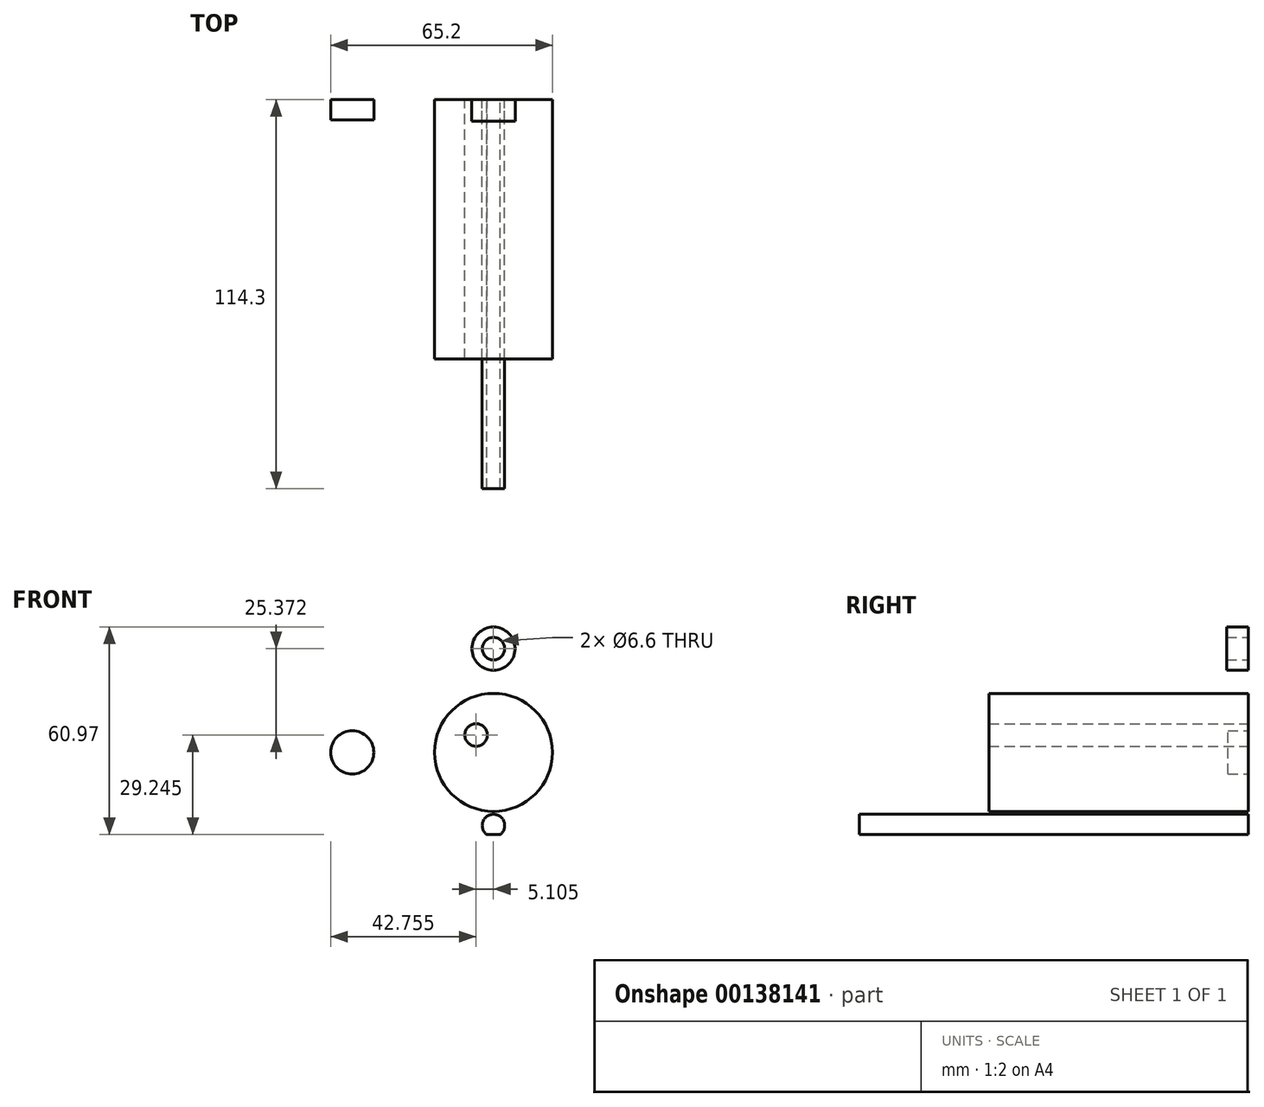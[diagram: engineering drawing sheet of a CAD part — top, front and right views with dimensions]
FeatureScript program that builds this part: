
annotation { "Feature Type Name" : "Feature", "Feature Type Description" : "" }
export const myFeature = defineFeature(function(context is Context, id is Id, definition is map)
    precondition{}
    {
        {
            var Q0;
            Q0=qCreatedBy(makeId("Front.planeOp"),FACE);
            var sketch = newSketch(context, id + "F0", { "sketchPlane" : qUnion([Q0])});
            skCircle(sketch, "E0", {"center": v(0, 0) * mm, "radius": 17.34 * mm});
            skLineSegment(sketch, "E1", {"start": v(0, 0) * mm, "end": v(0, 17.34) * mm, "construction": true});
            skLineSegment(sketch, "E2", {"start": v(0, 0) * mm, "end": v(0, -17.34) * mm, "construction": true});
            skLineSegment(sketch, "E3", {"start": v(-17.34, 0) * mm, "end": v(17.34, 0) * mm, "construction": true});
            skLineSegment(sketch, "E4", {"start": v(-5.1, 0) * mm, "end": v(-5.1, 5.1) * mm});
            skLineSegment(sketch, "E5", {"start": v(-5.1, 5.1) * mm, "end": v(0, 5.1) * mm, "construction": true});
            skCircle(sketch, "E6", {"center": v(-5.1, 5.1) * mm, "radius": 3.3 * mm});
            skSolve(sketch);
        }
        {
            var Q0;
            Q0=qCreatedBy(makeId("Front.planeOp"),FACE);
            var sketch = newSketch(context, id + "F1", { "sketchPlane" : qUnion([Q0])});
            skArc(sketch, "E7", {"start": v(1.98, -24.14) * mm, "mid": v(0, -18.2) * mm, "end": v(-1.98, -24.14) * mm});
            skLineSegment(sketch, "E8", {"start": v(-1.98, -24.14) * mm, "end": v(1.98, -24.14) * mm});
            skSolve(sketch);
        }
        {
            var Q0;
            Q0=makeQuery(id+"F0.imprint","IMPRINT",FACE,{"disambiguationData":[TD([[makeQuery(id+"F0.imprint","IMPRINT",EDGE,{"derivedFrom":sQuery(id+"F0.wireOp",EDGE,"E0")}),1.0]])]});
            extrude(context, id + "F2", {"entities" : qUnion([Q0]), "depth" : 76.2 * mm});
        }
        {
            var Q0;
            Q0=makeQuery(id+"F1.imprint","IMPRINT",FACE,{"disambiguationData":[TD([[makeQuery(id+"F1.imprint","IMPRINT",EDGE,{"derivedFrom":sQuery(id+"F1.wireOp",EDGE,"E7")}),1.0]])]});
            extrude(context, id + "F3", {"entities" : qUnion([Q0]), "depth" : 114.3 * mm});
        }
        {
            var Q0;
            Q0=qCreatedBy(makeId("Front.planeOp"),FACE);
            var sketch = newSketch(context, id + "F4", { "sketchPlane" : qUnion([Q0])});
            skCircle(sketch, "E9", {"center": v(0, 30.48) * mm, "radius": 6.35 * mm});
            skCircle(sketch, "E10", {"center": v(0, 30.48) * mm, "radius": 3.3 * mm});
            skSolve(sketch);
        }
        {
            var Q0;
            Q0=makeQuery(id+"F4.imprint","IMPRINT",FACE,{"disambiguationData":[TD([[makeQuery(id+"F4.imprint","IMPRINT",EDGE,{"derivedFrom":sQuery(id+"F4.wireOp",EDGE,"E9")}),1.0]])]});
            extrude(context, id + "F5", {"entities" : qUnion([Q0]), "depth" : 6.35 * mm});
        }
        {
            var Q0;
            Q0=qCreatedBy(makeId("Front.planeOp"),FACE);
            var sketch = newSketch(context, id + "F6", { "sketchPlane" : qUnion([Q0])});
            skCircle(sketch, "E11", {"center": v(-41.5, 0) * mm, "radius": 6.35 * mm});
            skSolve(sketch);
        }
        {
            var Q0;
            Q0=makeQuery(id+"F6.imprint","IMPRINT",FACE,{"disambiguationData":[TD([[makeQuery(id+"F6.imprint","IMPRINT",EDGE,{"derivedFrom":sQuery(id+"F6.wireOp",EDGE,"E11")}),1.0]])]});
            extrude(context, id + "F7", {"entities" : qUnion([Q0]), "depth" : 6 * mm});
        }
    });
